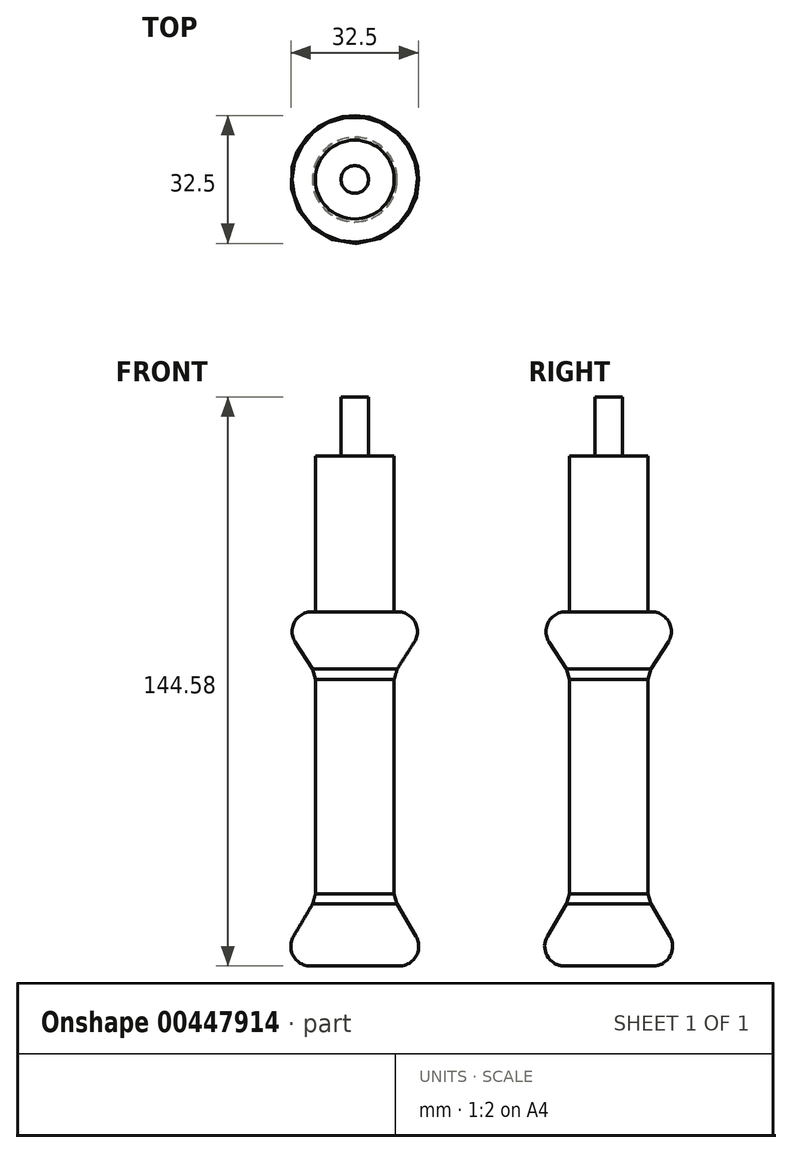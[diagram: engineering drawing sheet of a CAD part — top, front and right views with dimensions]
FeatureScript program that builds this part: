
annotation { "Feature Type Name" : "Feature", "Feature Type Description" : "" }
export const myFeature = defineFeature(function(context is Context, id is Id, definition is map)
    precondition{}
    {
        {
            var Q0;
            Q0=qCreatedBy(makeId("Front.planeOp"),FACE);
            var sketch = newSketch(context, id + "F0", { "sketchPlane" : qUnion([Q0])});
            skLineSegment(sketch, "E0", {"start": v(0, 55.37) * mm, "end": v(0, -74.21) * mm});
            skLineSegment(sketch, "E1", {"start": v(0, -74.21) * mm, "end": v(-20, -74.21) * mm});
            skLineSegment(sketch, "E2", {"start": v(-20, -74.21) * mm, "end": v(-10, -57.25) * mm});
            skLineSegment(sketch, "E3", {"start": v(-10, -57.25) * mm, "end": v(-10, 0) * mm});
            skLineSegment(sketch, "E4", {"start": v(-10, 0) * mm, "end": v(-20, 15.79) * mm});
            skLineSegment(sketch, "E5", {"start": v(-20, 15.79) * mm, "end": v(-10, 15.79) * mm});
            skLineSegment(sketch, "E6", {"start": v(-10, 15.79) * mm, "end": v(-10, 55.37) * mm});
            skLineSegment(sketch, "E7", {"start": v(-10, 55.37) * mm, "end": v(0, 55.37) * mm});
            skSolve(sketch);
        }
        {
            var Q0;
            Q0=makeQuery(id+"F0.imprint","IMPRINT",FACE,{"disambiguationData":[TD([[makeQuery(id+"F0.imprint","IMPRINT",EDGE,{"derivedFrom":sQuery(id+"F0.wireOp",EDGE,"E0")}),-1.0]])]});
            var Q1;
            Q1=sQuery(id+"F0.wireOp",EDGE,"E0");
            revolve(context, id + "F1", {"entities" : qUnion([Q0]), "axis" : qUnion([Q1]), "revolveType" : RevolveType.FULL});
        }
        {
            var Q0;
            Q0=makeQuery(id+"F1.opRevolve","SWEPT_EDGE",EDGE,{"disambiguationData":[OSD([sQuery(id+"F0.wireOp",EDGE,"E4"),sQuery(id+"F0.wireOp",EDGE,"E5")])]});
            var Q1;
            Q1=makeQuery(id+"F1.opRevolve","SWEPT_EDGE",EDGE,{"disambiguationData":[OSD([sQuery(id+"F0.wireOp",EDGE,"E1"),sQuery(id+"F0.wireOp",EDGE,"E2")])]});
            fillet(context, id + "F2", {"entities" : qUnion([Q0, Q1]), "radius" : 5 * mm, "tangentPropagation" : true, "allowEdgeOverflow" : false});
        }
        {
            var Q0;
            Q0=makeQuery(id+"F1.opRevolve","SWEPT_EDGE",EDGE,{"disambiguationData":[OSD([sQuery(id+"F0.wireOp",EDGE,"E3"),sQuery(id+"F0.wireOp",EDGE,"E4")])]});
            var Q1;
            Q1=makeQuery(id+"F1.opRevolve","SWEPT_EDGE",EDGE,{"disambiguationData":[OSD([sQuery(id+"F0.wireOp",EDGE,"E2"),sQuery(id+"F0.wireOp",EDGE,"E3")])]});
            chamfer(context, id + "F3", {"entities" : qUnion([Q0, Q1]), "width" : 5 * mm, "tangentPropagation" : true});
        }
        {
            var Q0;
            Q0=makeQuery(id+"F1.opRevolve","SWEPT_FACE",FACE,{"disambiguationData":[OSD([sQuery(id+"F0.wireOp",EDGE,"E7")])]});
            var sketch = newSketch(context, id + "F4", { "sketchPlane" : qUnion([Q0])});
            skCircle(sketch, "E8", {"center": v(0, 0) * mm, "radius": 3.5 * mm});
            skSolve(sketch);
        }
        {
            var Q0;
            Q0 = qSketchRegion(id + "F4", true);
            extrude(context, id + "F5", {"entities" : qUnion([Q0]), "operationType" : NewBodyOperationType.ADD, "depth" : 15 * mm});
        }
    });
